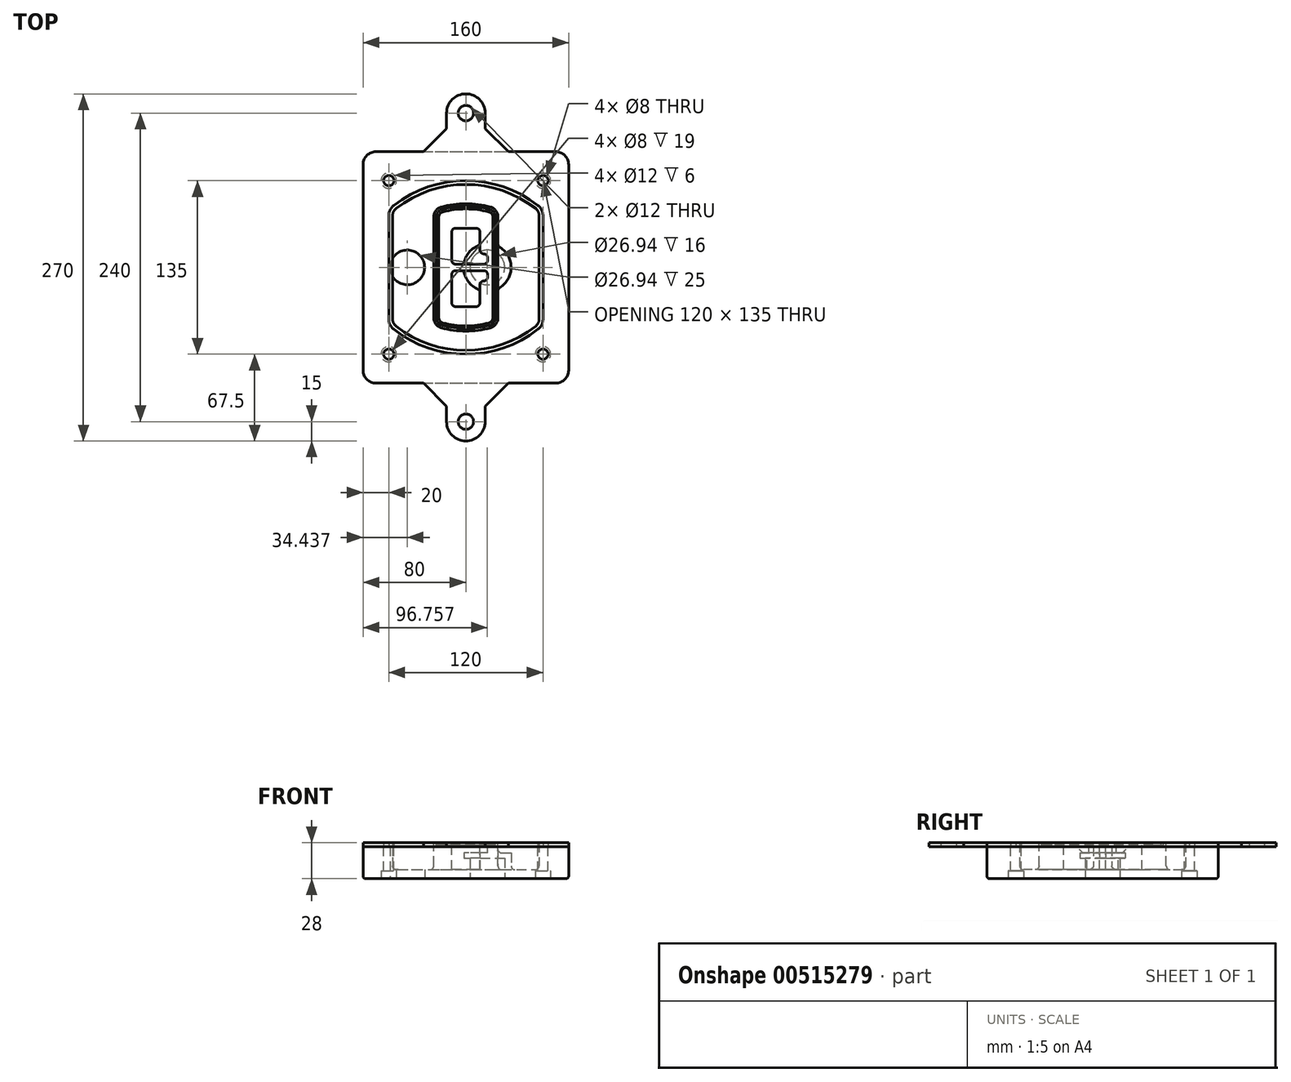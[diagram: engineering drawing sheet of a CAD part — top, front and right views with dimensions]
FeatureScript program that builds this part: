
annotation { "Feature Type Name" : "Feature", "Feature Type Description" : "" }
export const myFeature = defineFeature(function(context is Context, id is Id, definition is map)
    precondition{}
    {
        {
            var Q0;
            Q0=qCreatedBy(makeId("Top.planeOp"),FACE);
            var sketch = newSketch(context, id + "F0", { "sketchPlane" : qUnion([Q0])});
            skPoint(sketch, "E0.rect.middle", {"position": v(0, 0) * mm});
            skLineSegment(sketch, "E1.bottom", {"start": v(-70, -90) * mm, "end": v(70, -90) * mm});
            skLineSegment(sketch, "E1.top", {"start": v(-70, 90) * mm, "end": v(70, 90) * mm});
            skLineSegment(sketch, "E1.left", {"start": v(-80, -80) * mm, "end": v(-80, 80) * mm});
            skLineSegment(sketch, "E1.right", {"start": v(80, -80) * mm, "end": v(80, 80) * mm});
            skLineSegment(sketch, "E2", {"start": v(-80, 90) * mm, "end": v(80, -90) * mm, "construction": true});
            skLineSegment(sketch, "E3", {"start": v(80, 90) * mm, "end": v(-80, -90) * mm, "construction": true});
            skCircle(sketch, "E4", {"center": v(-60, 67.5) * mm, "radius": 4 * mm});
            skCircle(sketch, "E5", {"center": v(60, 67.5) * mm, "radius": 4 * mm});
            skCircle(sketch, "E6", {"center": v(60, -67.5) * mm, "radius": 4 * mm});
            skCircle(sketch, "E7", {"center": v(-60, -67.5) * mm, "radius": 4 * mm});
            skLineSegment(sketch, "E8", {"start": v(-60, 67.5) * mm, "end": v(60, 67.5) * mm, "construction": true});
            skLineSegment(sketch, "E9", {"start": v(60, 67.5) * mm, "end": v(60, -67.5) * mm, "construction": true});
            skLineSegment(sketch, "E10", {"start": v(60, -67.5) * mm, "end": v(-60, -67.5) * mm, "construction": true});
            skLineSegment(sketch, "E11", {"start": v(-60, -67.5) * mm, "end": v(-60, 67.5) * mm, "construction": true});
            skLineSegment(sketch, "E12", {"start": v(-60, 40.3) * mm, "end": v(-60, -40.3) * mm});
            skLineSegment(sketch, "E13", {"start": v(60, 40.3) * mm, "end": v(60, -40.3) * mm});
            skArc(sketch, "E14", {"start": v(56.15, 48.18) * mm, "mid": v(0, 67.5) * mm, "end": v(-56.15, 48.18) * mm});
            skArc(sketch, "E15", {"start": v(-56.15, -48.18) * mm, "mid": v(0, -67.5) * mm, "end": v(56.15, -48.18) * mm});
            skLineSegment(sketch, "E16", {"start": v(-60, 0) * mm, "end": v(60, 0) * mm, "construction": true});
            skPoint(sketch, "E17.visualSharp", {"position": v(-60, -45) * mm});
            skArc(sketch, "E17.filletArc", {"start": v(-60, -40.3) * mm, "mid": v(-58.99, -44.68) * mm, "end": v(-56.15, -48.18) * mm});
            skPoint(sketch, "E18.visualSharp", {"position": v(-60, 45) * mm});
            skArc(sketch, "E18.filletArc", {"start": v(-56.15, 48.18) * mm, "mid": v(-58.99, 44.68) * mm, "end": v(-60, 40.3) * mm});
            skPoint(sketch, "E19.visualSharp", {"position": v(60, 45) * mm});
            skArc(sketch, "E19.filletArc", {"start": v(60, 40.3) * mm, "mid": v(58.99, 44.68) * mm, "end": v(56.15, 48.18) * mm});
            skPoint(sketch, "E20.visualSharp", {"position": v(60, -45) * mm});
            skArc(sketch, "E20.filletArc", {"start": v(56.15, -48.18) * mm, "mid": v(58.99, -44.68) * mm, "end": v(60, -40.3) * mm});
            skPoint(sketch, "E21.visualSharp", {"position": v(-80, 90) * mm});
            skArc(sketch, "E21.filletArc", {"start": v(-70, 90) * mm, "mid": v(-77.07, 87.07) * mm, "end": v(-80, 80) * mm});
            skPoint(sketch, "E22.visualSharp", {"position": v(80, 90) * mm});
            skArc(sketch, "E22.filletArc", {"start": v(80, 80) * mm, "mid": v(77.07, 87.07) * mm, "end": v(70, 90) * mm});
            skPoint(sketch, "E23.visualSharp", {"position": v(80, -90) * mm});
            skArc(sketch, "E23.filletArc", {"start": v(70, -90) * mm, "mid": v(77.07, -87.07) * mm, "end": v(80, -80) * mm});
            skPoint(sketch, "E24.visualSharp", {"position": v(-80, -90) * mm});
            skArc(sketch, "E24.filletArc", {"start": v(-80, -80) * mm, "mid": v(-77.07, -87.07) * mm, "end": v(-70, -90) * mm});
            skArc(sketch, "E25.0", {"start": v(57, 40.3) * mm, "mid": v(56.3, 43.36) * mm, "end": v(54.3, 45.81) * mm});
            skLineSegment(sketch, "E25.1", {"start": v(57, 40.3) * mm, "end": v(57, -40.3) * mm});
            skArc(sketch, "E25.2", {"start": v(54.3, -45.81) * mm, "mid": v(56.3, -43.36) * mm, "end": v(57, -40.3) * mm});
            skArc(sketch, "E25.3", {"start": v(-54.3, -45.81) * mm, "mid": v(0, -64.5) * mm, "end": v(54.3, -45.81) * mm});
            skArc(sketch, "E25.4", {"start": v(-57, -40.3) * mm, "mid": v(-56.3, -43.36) * mm, "end": v(-54.3, -45.81) * mm});
            skArc(sketch, "E25.5", {"start": v(54.3, 45.81) * mm, "mid": v(0, 64.5) * mm, "end": v(-54.3, 45.81) * mm});
            skLineSegment(sketch, "E25.6", {"start": v(-57, 40.3) * mm, "end": v(-57, -40.3) * mm});
            skArc(sketch, "E25.7", {"start": v(-54.3, 45.81) * mm, "mid": v(-56.3, 43.36) * mm, "end": v(-57, 40.3) * mm});
            skArc(sketch, "E26.0", {"start": v(-58.62, 51.33) * mm, "mid": v(-62.58, 46.43) * mm, "end": v(-64, 40.3) * mm});
            skArc(sketch, "E26.1", {"start": v(58.62, 51.33) * mm, "mid": v(0, 71.5) * mm, "end": v(-58.62, 51.33) * mm});
            skArc(sketch, "E26.2", {"start": v(64, 40.3) * mm, "mid": v(62.58, 46.43) * mm, "end": v(58.62, 51.33) * mm});
            skLineSegment(sketch, "E26.3", {"start": v(64, 40.3) * mm, "end": v(64, -40.3) * mm});
            skArc(sketch, "E26.4", {"start": v(58.62, -51.33) * mm, "mid": v(62.58, -46.43) * mm, "end": v(64, -40.3) * mm});
            skLineSegment(sketch, "E26.5", {"start": v(-64, 40.3) * mm, "end": v(-64, -40.3) * mm});
            skArc(sketch, "E26.6", {"start": v(-58.62, -51.33) * mm, "mid": v(0, -71.5) * mm, "end": v(58.62, -51.33) * mm});
            skArc(sketch, "E26.7", {"start": v(-64, -40.3) * mm, "mid": v(-62.58, -46.43) * mm, "end": v(-58.62, -51.33) * mm});
            skSolve(sketch);
        }
        {
            var Q0;
            Q0=makeQuery(id+"F0.imprint","IMPRINT",FACE,{"disambiguationData":[TD([[makeQuery(id+"F0.imprint","IMPRINT",EDGE,{"derivedFrom":sQuery(id+"F0.wireOp",EDGE,"E1.bottom")}),1.0]])]});
            var Q1;
            Q1=makeQuery(id+"F0.imprint","IMPRINT",FACE,{"disambiguationData":[TD([[makeQuery(id+"F0.imprint","IMPRINT",EDGE,{"derivedFrom":sQuery(id+"F0.wireOp",EDGE,"E12")}),1.0]])]});
            var Q2;
            Q2=makeQuery(id+"F0.imprint","IMPRINT",FACE,{"disambiguationData":[TD([[makeQuery(id+"F0.imprint","IMPRINT",EDGE,{"derivedFrom":sQuery(id+"F0.wireOp",EDGE,"E25.0")}),1.0]])]});
            var Q3;
            Q3=makeQuery(id+"F0.imprint","IMPRINT",FACE,{"disambiguationData":[TD([[makeQuery(id+"F0.imprint","IMPRINT",EDGE,{"derivedFrom":sQuery(id+"F0.wireOp",EDGE,"E12")}),-1.0]])]});
            extrude(context, id + "F1", {"entities" : qUnion([Q0, Q1, Q2, Q3]), "oppositeDirection" : true, "depth" : 25 * mm});
        }
        {
            var Q0;
            Q0=makeQuery(id+"F0.imprint","IMPRINT",FACE,{"disambiguationData":[TD([[makeQuery(id+"F0.imprint","IMPRINT",EDGE,{"derivedFrom":sQuery(id+"F0.wireOp",EDGE,"E12")}),1.0]])]});
            extrude(context, id + "F2", {"entities" : qUnion([Q0]), "operationType" : NewBodyOperationType.ADD, "depth" : 3 * mm});
        }
        {
            var Q0;
            Q0=makeQuery(id+"F0.imprint","IMPRINT",FACE,{"disambiguationData":[TD([[makeQuery(id+"F0.imprint","IMPRINT",EDGE,{"derivedFrom":sQuery(id+"F0.wireOp",EDGE,"E25.0")}),1.0]])]});
            extrude(context, id + "F3", {"entities" : qUnion([Q0]), "operationType" : NewBodyOperationType.REMOVE, "oppositeDirection" : true, "depth" : 18 * mm});
        }
        {
            var Q0;
            Q0=makeQuery(id+"F2.opExtrude","CAP_FACE",FACE,{"disambiguationData":[OSD([sQuery(id+"F0.wireOp",EDGE,"E12"),sQuery(id+"F0.wireOp",EDGE,"E13"),sQuery(id+"F0.wireOp",EDGE,"E14"),sQuery(id+"F0.wireOp",EDGE,"E15"),sQuery(id+"F0.wireOp",EDGE,"E17.filletArc"),sQuery(id+"F0.wireOp",EDGE,"E18.filletArc"),sQuery(id+"F0.wireOp",EDGE,"E19.filletArc"),sQuery(id+"F0.wireOp",EDGE,"E20.filletArc"),sQuery(id+"F0.wireOp",EDGE,"E25.0"),sQuery(id+"F0.wireOp",EDGE,"E25.1"),sQuery(id+"F0.wireOp",EDGE,"E25.2"),sQuery(id+"F0.wireOp",EDGE,"E25.3"),sQuery(id+"F0.wireOp",EDGE,"E25.4"),sQuery(id+"F0.wireOp",EDGE,"E25.5"),sQuery(id+"F0.wireOp",EDGE,"E25.6"),sQuery(id+"F0.wireOp",EDGE,"E25.7")])],"isStart":false});
            var sketch = newSketch(context, id + "F4", { "sketchPlane" : qUnion([Q0])});
            skArc(sketch, "E27.0", {"start": v(-19.08, -46.97) * mm, "mid": v(0, -49.5) * mm, "end": v(19.08, -46.97) * mm});
            skArc(sketch, "E28.0", {"start": v(19.08, 46.97) * mm, "mid": v(0, 49.5) * mm, "end": v(-19.08, 46.97) * mm});
            skLineSegment(sketch, "E29", {"start": v(-25, 39.25) * mm, "end": v(-25, -39.25) * mm});
            skLineSegment(sketch, "E30", {"start": v(25, 39.25) * mm, "end": v(25, -39.25) * mm});
            skLineSegment(sketch, "E31", {"start": v(-25, 45.1) * mm, "end": v(25, 45.1) * mm, "construction": true});
            skLineSegment(sketch, "E32", {"start": v(-25, -45.1) * mm, "end": v(25, -45.1) * mm, "construction": true});
            skPoint(sketch, "E33.visualSharp", {"position": v(-25, 45.1) * mm});
            skArc(sketch, "E33.filletArc", {"start": v(-19.08, 46.97) * mm, "mid": v(-23.35, 44.11) * mm, "end": v(-25, 39.25) * mm});
            skPoint(sketch, "E34.visualSharp", {"position": v(25, 45.1) * mm});
            skArc(sketch, "E34.filletArc", {"start": v(25, 39.25) * mm, "mid": v(23.35, 44.11) * mm, "end": v(19.08, 46.97) * mm});
            skPoint(sketch, "E35.visualSharp", {"position": v(25, -45.1) * mm});
            skArc(sketch, "E35.filletArc", {"start": v(19.08, -46.97) * mm, "mid": v(23.35, -44.11) * mm, "end": v(25, -39.25) * mm});
            skPoint(sketch, "E36.visualSharp", {"position": v(-25, -45.1) * mm});
            skArc(sketch, "E36.filletArc", {"start": v(-25, -39.25) * mm, "mid": v(-23.35, -44.11) * mm, "end": v(-19.08, -46.97) * mm});
            skArc(sketch, "E37.0", {"start": v(54.3, 45.81) * mm, "mid": v(0, 64.5) * mm, "end": v(-54.3, 45.81) * mm});
            skArc(sketch, "E37.1", {"start": v(-54.3, 45.81) * mm, "mid": v(-56.3, 43.36) * mm, "end": v(-57, 40.3) * mm});
            skLineSegment(sketch, "E37.2", {"start": v(-57, 40.3) * mm, "end": v(-57, -40.3) * mm});
            skArc(sketch, "E37.3", {"start": v(-57, -40.3) * mm, "mid": v(-56.3, -43.36) * mm, "end": v(-54.3, -45.81) * mm});
            skArc(sketch, "E37.4", {"start": v(-54.3, -45.81) * mm, "mid": v(0, -64.5) * mm, "end": v(54.3, -45.81) * mm});
            skArc(sketch, "E37.5", {"start": v(54.3, -45.81) * mm, "mid": v(56.3, -43.36) * mm, "end": v(57, -40.3) * mm});
            skLineSegment(sketch, "E37.6", {"start": v(57, 40.3) * mm, "end": v(57, -40.3) * mm});
            skArc(sketch, "E37.7", {"start": v(57, 40.3) * mm, "mid": v(56.3, 43.36) * mm, "end": v(54.3, 45.81) * mm});
            skLineSegment(sketch, "E38.0", {"start": v(23, 39.25) * mm, "end": v(23, -39.25) * mm});
            skArc(sketch, "E38.1", {"start": v(18.56, -45.04) * mm, "mid": v(21.76, -42.9) * mm, "end": v(23, -39.25) * mm});
            skArc(sketch, "E38.2", {"start": v(-18.56, -45.04) * mm, "mid": v(0, -47.5) * mm, "end": v(18.56, -45.04) * mm});
            skArc(sketch, "E38.3", {"start": v(-23, -39.25) * mm, "mid": v(-21.76, -42.9) * mm, "end": v(-18.56, -45.04) * mm});
            skLineSegment(sketch, "E38.4", {"start": v(-23, 39.25) * mm, "end": v(-23, -39.25) * mm});
            skArc(sketch, "E38.5", {"start": v(23, 39.25) * mm, "mid": v(21.76, 42.9) * mm, "end": v(18.56, 45.04) * mm});
            skArc(sketch, "E38.6", {"start": v(-18.56, 45.04) * mm, "mid": v(-21.76, 42.9) * mm, "end": v(-23, 39.25) * mm});
            skArc(sketch, "E38.7", {"start": v(18.56, 45.04) * mm, "mid": v(0, 47.5) * mm, "end": v(-18.56, 45.04) * mm});
            skArc(sketch, "E39.0", {"start": v(21, 39.25) * mm, "mid": v(20.18, 41.68) * mm, "end": v(18.04, 43.1) * mm});
            skLineSegment(sketch, "E39.1", {"start": v(21, 39.25) * mm, "end": v(21, -39.25) * mm});
            skArc(sketch, "E39.2", {"start": v(18.04, -43.1) * mm, "mid": v(20.18, -41.68) * mm, "end": v(21, -39.25) * mm});
            skArc(sketch, "E39.3", {"start": v(-18.04, -43.1) * mm, "mid": v(0, -45.5) * mm, "end": v(18.04, -43.1) * mm});
            skArc(sketch, "E39.4", {"start": v(-21, -39.25) * mm, "mid": v(-20.18, -41.68) * mm, "end": v(-18.04, -43.1) * mm});
            skArc(sketch, "E39.5", {"start": v(18.04, 43.1) * mm, "mid": v(0, 45.5) * mm, "end": v(-18.04, 43.1) * mm});
            skLineSegment(sketch, "E39.6", {"start": v(-21, 39.25) * mm, "end": v(-21, -39.25) * mm});
            skArc(sketch, "E39.7", {"start": v(-18.04, 43.1) * mm, "mid": v(-20.18, 41.68) * mm, "end": v(-21, 39.25) * mm});
            skLineSegment(sketch, "E40", {"start": v(-25, 0) * mm, "end": v(25, 0) * mm, "construction": true});
            skLineSegment(sketch, "E41", {"start": v(-11, 5.5) * mm, "end": v(-11, 27.5) * mm});
            skLineSegment(sketch, "E42", {"start": v(-8, 30.5) * mm, "end": v(8, 30.5) * mm});
            skLineSegment(sketch, "E43", {"start": v(11, 27.5) * mm, "end": v(11, 13.5) * mm});
            skLineSegment(sketch, "E44", {"start": v(14, 10.5) * mm, "end": v(14, 10.5) * mm});
            skLineSegment(sketch, "E45", {"start": v(17, 7.5) * mm, "end": v(17, 5.5) * mm});
            skLineSegment(sketch, "E46", {"start": v(14, 2.5) * mm, "end": v(-8, 2.5) * mm});
            skPoint(sketch, "E47.visualSharp", {"position": v(-11, 30.5) * mm});
            skArc(sketch, "E47.filletArc", {"start": v(-8, 30.5) * mm, "mid": v(-10.12, 29.62) * mm, "end": v(-11, 27.5) * mm});
            skPoint(sketch, "E48.visualSharp", {"position": v(11, 30.5) * mm});
            skArc(sketch, "E48.filletArc", {"start": v(11, 27.5) * mm, "mid": v(10.12, 29.62) * mm, "end": v(8, 30.5) * mm});
            skPoint(sketch, "E49.visualSharp", {"position": v(11, 10.5) * mm});
            skArc(sketch, "E49.filletArc", {"start": v(11, 13.5) * mm, "mid": v(11.88, 11.38) * mm, "end": v(14, 10.5) * mm});
            skPoint(sketch, "E50.visualSharp", {"position": v(17, 10.5) * mm});
            skArc(sketch, "E50.filletArc", {"start": v(17, 7.5) * mm, "mid": v(16.12, 9.62) * mm, "end": v(14, 10.5) * mm});
            skPoint(sketch, "E51.visualSharp", {"position": v(17, 2.5) * mm});
            skArc(sketch, "E51.filletArc", {"start": v(14, 2.5) * mm, "mid": v(16.12, 3.38) * mm, "end": v(17, 5.5) * mm});
            skPoint(sketch, "E52.visualSharp", {"position": v(-11, 2.5) * mm});
            skArc(sketch, "E52.filletArc", {"start": v(-11, 5.5) * mm, "mid": v(-10.12, 3.38) * mm, "end": v(-8, 2.5) * mm});
            skLineSegment(sketch, "E53.0.MirrorCS", {"start": v(14, -2.5) * mm, "end": v(-8, -2.5) * mm});
            skArc(sketch, "E54.0.MirrorCS", {"start": v(-11, -5.5) * mm, "mid": v(-10.12, -3.38) * mm, "end": v(-8, -2.5) * mm});
            skLineSegment(sketch, "E55.0.MirrorCS", {"start": v(-11, -5.5) * mm, "end": v(-11, -27.5) * mm});
            skArc(sketch, "E56.0.MirrorCS", {"start": v(-8, -30.5) * mm, "mid": v(-10.12, -29.62) * mm, "end": v(-11, -27.5) * mm});
            skLineSegment(sketch, "E57.0.MirrorCS", {"start": v(-8, -30.5) * mm, "end": v(8, -30.5) * mm});
            skArc(sketch, "E58.0.MirrorCS", {"start": v(11, -27.5) * mm, "mid": v(10.12, -29.62) * mm, "end": v(8, -30.5) * mm});
            skLineSegment(sketch, "E59.0.MirrorCS", {"start": v(11, -27.5) * mm, "end": v(11, -13.5) * mm});
            skArc(sketch, "E60.0.MirrorCS", {"start": v(11, -13.5) * mm, "mid": v(11.88, -11.38) * mm, "end": v(14, -10.5) * mm});
            skArc(sketch, "E61.0.MirrorCS", {"start": v(17, -7.5) * mm, "mid": v(16.12, -9.62) * mm, "end": v(14, -10.5) * mm});
            skLineSegment(sketch, "E62.0.MirrorCS", {"start": v(17, -7.5) * mm, "end": v(17, -5.5) * mm});
            skArc(sketch, "E63.0.MirrorCS", {"start": v(14, -2.5) * mm, "mid": v(16.12, -3.38) * mm, "end": v(17, -5.5) * mm});
            skSolve(sketch);
        }
        {
            var Q0;
            Q0=makeQuery(id+"F4.imprint","IMPRINT",FACE,{"disambiguationData":[TD([[makeQuery(id+"F4.imprint","IMPRINT",EDGE,{"derivedFrom":sQuery(id+"F4.wireOp",EDGE,"E27.0")}),1.0]])]});
            var Q1;
            Q1=makeQuery(id+"F4.imprint","IMPRINT",FACE,{"disambiguationData":[TD([[makeQuery(id+"F4.imprint","IMPRINT",EDGE,{"derivedFrom":sQuery(id+"F4.wireOp",EDGE,"E38.0")}),-1.0]])]});
            var Q2;
            Q2=makeQuery(id+"F4.imprint","IMPRINT",FACE,{"disambiguationData":[TD([[makeQuery(id+"F4.imprint","IMPRINT",EDGE,{"derivedFrom":sQuery(id+"F4.wireOp",EDGE,"E39.0")}),1.0]])]});
            extrude(context, id + "F5", {"entities" : qUnion([Q0, Q1, Q2]), "operationType" : NewBodyOperationType.ADD, "endBound" : BoundingType.UP_TO_NEXT, "oppositeDirection" : true, "depth" : 25 * mm});
        }
        {
            var Q0;
            Q0=makeQuery(id+"F4.imprint","IMPRINT",FACE,{"disambiguationData":[TD([[makeQuery(id+"F4.imprint","IMPRINT",EDGE,{"derivedFrom":sQuery(id+"F4.wireOp",EDGE,"E38.0")}),-1.0]])]});
            extrude(context, id + "F6", {"entities" : qUnion([Q0]), "operationType" : NewBodyOperationType.REMOVE, "oppositeDirection" : true, "depth" : 2 * mm});
        }
        {
            var Q0;
            Q0=makeQuery(id+"F1.opExtrude","CAP_FACE",FACE,{"disambiguationData":[OSD([sQuery(id+"F0.wireOp",EDGE,"E1.bottom"),sQuery(id+"F0.wireOp",EDGE,"E1.top"),sQuery(id+"F0.wireOp",EDGE,"E1.left"),sQuery(id+"F0.wireOp",EDGE,"E1.right"),sQuery(id+"F0.wireOp",EDGE,"E4"),sQuery(id+"F0.wireOp",EDGE,"E5"),sQuery(id+"F0.wireOp",EDGE,"E6"),sQuery(id+"F0.wireOp",EDGE,"E7"),sQuery(id+"F0.wireOp",EDGE,"E21.filletArc"),sQuery(id+"F0.wireOp",EDGE,"E22.filletArc"),sQuery(id+"F0.wireOp",EDGE,"E23.filletArc"),sQuery(id+"F0.wireOp",EDGE,"E24.filletArc")])],"isStart":false});
            var sketch = newSketch(context, id + "F7", { "sketchPlane" : qUnion([Q0])});
            skCircle(sketch, "E64", {"center": v(16.76, 0) * mm, "radius": 13.47 * mm});
            skCircle(sketch, "E65", {"center": v(-45.56, 0) * mm, "radius": 13.47 * mm});
            skLineSegment(sketch, "E66", {"start": v(80, 0) * mm, "end": v(-80, 0) * mm});
            skCircle(sketch, "E67", {"center": v(16.76, 0) * mm, "radius": 18.47 * mm});
            skCircle(sketch, "E68", {"center": v(60, -67.5) * mm, "radius": 6 * mm});
            skCircle(sketch, "E69", {"center": v(-60, -67.5) * mm, "radius": 6 * mm});
            skCircle(sketch, "E70", {"center": v(-60, 67.5) * mm, "radius": 6 * mm});
            skCircle(sketch, "E71", {"center": v(60, 67.5) * mm, "radius": 6 * mm});
            skSolve(sketch);
        }
        {
            var Q0;
            {var subQ1=sQuery(id+"F7.wireOp",EDGE,"E66");var subQ4=sQuery(id+"F7.wireOp",EDGE,"E64");var subQ6=makeQuery(id+"F7.imprint","INTERSECT",VERTEX,{"disambiguationData":[OD(0.0)],"derivedFrom":[subQ4,subQ1]});Q0=makeQuery(id+"F7.imprint","IMPRINT",FACE,{"disambiguationData":[TD([[makeQuery(id+"F7.imprint","IMPRINT",EDGE,{"disambiguationData":[TD([[subQ6,-1.0]])],"derivedFrom":subQ4}),-1.0]])]});}
            var Q1;
            {var subQ0=sQuery(id+"F7.wireOp",EDGE,"E66");var subQ1=sQuery(id+"F7.wireOp",EDGE,"E64");var subQ3=makeQuery(id+"F7.imprint","INTERSECT",VERTEX,{"disambiguationData":[OD(0.0)],"derivedFrom":[subQ1,subQ0]});Q1=makeQuery(id+"F7.imprint","IMPRINT",FACE,{"disambiguationData":[TD([[makeQuery(id+"F7.imprint","IMPRINT",EDGE,{"disambiguationData":[TD([[subQ3,-1.0]])],"derivedFrom":subQ1}),1.0]])]});}
            var Q2;
            {var subQ0=sQuery(id+"F7.wireOp",EDGE,"E66");var subQ1=sQuery(id+"F7.wireOp",EDGE,"E64");var subQ3=makeQuery(id+"F7.imprint","INTERSECT",VERTEX,{"disambiguationData":[OD(0.0)],"derivedFrom":[subQ1,subQ0]});Q2=makeQuery(id+"F7.imprint","IMPRINT",FACE,{"disambiguationData":[TD([[makeQuery(id+"F7.imprint","IMPRINT",EDGE,{"disambiguationData":[TD([[subQ3,1.0]])],"derivedFrom":subQ1}),1.0]])]});}
            var Q3;
            {var subQ1=sQuery(id+"F7.wireOp",EDGE,"E66");var subQ4=sQuery(id+"F7.wireOp",EDGE,"E64");var subQ6=makeQuery(id+"F7.imprint","INTERSECT",VERTEX,{"disambiguationData":[OD(0.0)],"derivedFrom":[subQ4,subQ1]});Q3=makeQuery(id+"F7.imprint","IMPRINT",FACE,{"disambiguationData":[TD([[makeQuery(id+"F7.imprint","IMPRINT",EDGE,{"disambiguationData":[TD([[subQ6,1.0]])],"derivedFrom":subQ4}),-1.0]])]});}
            extrude(context, id + "F8", {"entities" : qUnion([Q0, Q1, Q2, Q3]), "operationType" : NewBodyOperationType.ADD, "oppositeDirection" : true, "depth" : 20 * mm});
        }
        {
            var Q0;
            {var subQ0=sQuery(id+"F7.wireOp",EDGE,"E66");var subQ1=sQuery(id+"F7.wireOp",EDGE,"E64");var subQ3=makeQuery(id+"F7.imprint","INTERSECT",VERTEX,{"disambiguationData":[OD(0.0)],"derivedFrom":[subQ1,subQ0]});Q0=makeQuery(id+"F7.imprint","IMPRINT",FACE,{"disambiguationData":[TD([[makeQuery(id+"F7.imprint","IMPRINT",EDGE,{"disambiguationData":[TD([[subQ3,-1.0]])],"derivedFrom":subQ1}),1.0]])]});}
            var Q1;
            {var subQ0=sQuery(id+"F7.wireOp",EDGE,"E66");var subQ1=sQuery(id+"F7.wireOp",EDGE,"E64");var subQ3=makeQuery(id+"F7.imprint","INTERSECT",VERTEX,{"disambiguationData":[OD(0.0)],"derivedFrom":[subQ1,subQ0]});Q1=makeQuery(id+"F7.imprint","IMPRINT",FACE,{"disambiguationData":[TD([[makeQuery(id+"F7.imprint","IMPRINT",EDGE,{"disambiguationData":[TD([[subQ3,1.0]])],"derivedFrom":subQ1}),1.0]])]});}
            extrude(context, id + "F9", {"entities" : qUnion([Q0, Q1]), "operationType" : NewBodyOperationType.REMOVE, "oppositeDirection" : true, "depth" : 16 * mm});
        }
        {
            var Q0;
            {var subQ0=sQuery(id+"F7.wireOp",EDGE,"E66");var subQ1=sQuery(id+"F7.wireOp",EDGE,"E65");var subQ3=makeQuery(id+"F7.imprint","INTERSECT",VERTEX,{"disambiguationData":[OD(0.0)],"derivedFrom":[subQ1,subQ0]});Q0=makeQuery(id+"F7.imprint","IMPRINT",FACE,{"disambiguationData":[TD([[makeQuery(id+"F7.imprint","IMPRINT",EDGE,{"disambiguationData":[TD([[subQ3,-1.0]])],"derivedFrom":subQ1}),1.0]])]});}
            var Q1;
            {var subQ0=sQuery(id+"F7.wireOp",EDGE,"E66");var subQ1=sQuery(id+"F7.wireOp",EDGE,"E65");var subQ3=makeQuery(id+"F7.imprint","INTERSECT",VERTEX,{"disambiguationData":[OD(0.0)],"derivedFrom":[subQ1,subQ0]});Q1=makeQuery(id+"F7.imprint","IMPRINT",FACE,{"disambiguationData":[TD([[makeQuery(id+"F7.imprint","IMPRINT",EDGE,{"disambiguationData":[TD([[subQ3,1.0]])],"derivedFrom":subQ1}),1.0]])]});}
            extrude(context, id + "F10", {"entities" : qUnion([Q0, Q1]), "operationType" : NewBodyOperationType.REMOVE, "oppositeDirection" : true, "depth" : 25 * mm});
        }
        {
            var Q0;
            Q0=makeQuery(id+"F7.imprint","IMPRINT",FACE,{"disambiguationData":[TD([[makeQuery(id+"F7.imprint","IMPRINT",EDGE,{"derivedFrom":sQuery(id+"F7.wireOp",EDGE,"E68")}),1.0]])]});
            var Q1;
            Q1=makeQuery(id+"F7.imprint","IMPRINT",FACE,{"disambiguationData":[TD([[makeQuery(id+"F7.imprint","IMPRINT",EDGE,{"derivedFrom":makeQuery(id+"F1.opExtrude","CAP_EDGE",EDGE,{"disambiguationData":[OSD([sQuery(id+"F0.wireOp",EDGE,"E5")])],"isStart":false})}),-1.0]])]});
            var Q2;
            Q2=makeQuery(id+"F7.imprint","IMPRINT",FACE,{"disambiguationData":[TD([[makeQuery(id+"F7.imprint","IMPRINT",EDGE,{"derivedFrom":sQuery(id+"F7.wireOp",EDGE,"E69")}),1.0]])]});
            var Q3;
            Q3=makeQuery(id+"F7.imprint","IMPRINT",FACE,{"disambiguationData":[TD([[makeQuery(id+"F7.imprint","IMPRINT",EDGE,{"derivedFrom":makeQuery(id+"F1.opExtrude","CAP_EDGE",EDGE,{"disambiguationData":[OSD([sQuery(id+"F0.wireOp",EDGE,"E4")])],"isStart":false})}),-1.0]])]});
            var Q4;
            Q4=makeQuery(id+"F7.imprint","IMPRINT",FACE,{"disambiguationData":[TD([[makeQuery(id+"F7.imprint","IMPRINT",EDGE,{"derivedFrom":sQuery(id+"F7.wireOp",EDGE,"E70")}),1.0]])]});
            var Q5;
            Q5=makeQuery(id+"F7.imprint","IMPRINT",FACE,{"disambiguationData":[TD([[makeQuery(id+"F7.imprint","IMPRINT",EDGE,{"derivedFrom":makeQuery(id+"F1.opExtrude","CAP_EDGE",EDGE,{"disambiguationData":[OSD([sQuery(id+"F0.wireOp",EDGE,"E7")])],"isStart":false})}),-1.0]])]});
            var Q6;
            Q6=makeQuery(id+"F7.imprint","IMPRINT",FACE,{"disambiguationData":[TD([[makeQuery(id+"F7.imprint","IMPRINT",EDGE,{"derivedFrom":sQuery(id+"F7.wireOp",EDGE,"E71")}),1.0]])]});
            var Q7;
            Q7=makeQuery(id+"F7.imprint","IMPRINT",FACE,{"disambiguationData":[TD([[makeQuery(id+"F7.imprint","IMPRINT",EDGE,{"derivedFrom":makeQuery(id+"F1.opExtrude","CAP_EDGE",EDGE,{"disambiguationData":[OSD([sQuery(id+"F0.wireOp",EDGE,"E6")])],"isStart":false})}),-1.0]])]});
            extrude(context, id + "F11", {"entities" : qUnion([Q0, Q1, Q2, Q3, Q4, Q5, Q6, Q7]), "operationType" : NewBodyOperationType.REMOVE, "oppositeDirection" : true, "depth" : 6 * mm});
        }
        {
            var Q0;
            Q0=makeQuery(id+"F9.boolean.opBoolean","COPY",FACE,{"derivedFrom":makeQuery(id+"F9.opExtrude","CAP_FACE",FACE,{"disambiguationData":[OSD([sQuery(id+"F7.wireOp",EDGE,"E64")])],"isStart":false})});
            var sketch = newSketch(context, id + "F12", { "sketchPlane" : qUnion([Q0])});
            skArc(sketch, "E72.0", {"start": v(11, 17.55) * mm, "mid": v(2.57, 11.82) * mm, "end": v(-1.54, 2.5) * mm});
            skArc(sketch, "E72.1", {"start": v(-1.54, -2.5) * mm, "mid": v(2.57, -11.82) * mm, "end": v(11, -17.55) * mm});
            skLineSegment(sketch, "E73", {"start": v(-1.54, -2.5) * mm, "end": v(14, -2.5) * mm});
            skLineSegment(sketch, "E74.0", {"start": v(14, 2.5) * mm, "end": v(-1.54, 2.5) * mm});
            skArc(sketch, "E74.1", {"start": v(14, 2.5) * mm, "mid": v(16.12, 3.38) * mm, "end": v(17, 5.5) * mm});
            skLineSegment(sketch, "E74.2", {"start": v(17, 7.5) * mm, "end": v(17, 5.5) * mm});
            skArc(sketch, "E74.3", {"start": v(17, 7.5) * mm, "mid": v(16.12, 9.62) * mm, "end": v(14, 10.5) * mm});
            skArc(sketch, "E74.4", {"start": v(11, 13.5) * mm, "mid": v(11.88, 11.38) * mm, "end": v(14, 10.5) * mm});
            skLineSegment(sketch, "E74.5", {"start": v(11, 17.55) * mm, "end": v(11, 13.5) * mm});
            skLineSegment(sketch, "E74.7", {"start": v(14, -2.5) * mm, "end": v(-1.54, -2.5) * mm});
            skArc(sketch, "E74.8", {"start": v(14, -2.5) * mm, "mid": v(16.12, -3.38) * mm, "end": v(17, -5.5) * mm});
            skLineSegment(sketch, "E74.9", {"start": v(17, -7.5) * mm, "end": v(17, -5.5) * mm});
            skArc(sketch, "E74.10", {"start": v(17, -7.5) * mm, "mid": v(16.12, -9.62) * mm, "end": v(14, -10.5) * mm});
            skArc(sketch, "E74.11", {"start": v(11, -13.5) * mm, "mid": v(11.88, -11.38) * mm, "end": v(14, -10.5) * mm});
            skLineSegment(sketch, "E74.12", {"start": v(11, -17.55) * mm, "end": v(11, -13.5) * mm});
            skPoint(sketch, "E75.orphan", {"position": v(11, -27.5) * mm});
            skPoint(sketch, "E76.orphan", {"position": v(-8, -2.5) * mm});
            skPoint(sketch, "E77.orphan", {"position": v(-8, 2.5) * mm});
            skPoint(sketch, "E78.orphan", {"position": v(11, 27.5) * mm});
            skSolve(sketch);
        }
        {
            var Q0;
            {var subQ7=sQuery(id+"F12.wireOp",EDGE,"E72.0");var subQ14=sQuery(id+"F12.wireOp",EDGE,"E72.1");var subQ16=sQuery(id+"F12.wireOp",EDGE,"E74.1");var subQ18=sQuery(id+"F12.wireOp",EDGE,"E74.8");Q0=qUnion([makeQuery(id+"F12.imprint","IMPRINT",FACE,{"disambiguationData":[TD([[makeQuery(id+"F12.imprint","IMPRINT",EDGE,{"derivedFrom":subQ7}),1.0]])]}),makeQuery(id+"F12.imprint","IMPRINT",FACE,{"disambiguationData":[TD([[makeQuery(id+"F12.imprint","IMPRINT",EDGE,{"derivedFrom":subQ14}),1.0]])]}),makeQuery(id+"F12.imprint","IMPRINT",FACE,{"disambiguationData":[TD([[makeQuery(id+"F12.imprint","IMPRINT",EDGE,{"derivedFrom":subQ16}),1.0]])]}),makeQuery(id+"F12.imprint","IMPRINT",FACE,{"disambiguationData":[TD([[makeQuery(id+"F12.imprint","IMPRINT",EDGE,{"derivedFrom":subQ18}),-1.0]])]})]);}
            var Q1;
            Q1=makeQuery(id+"F5.boolean.opBoolean","SPLIT",FACE,{"disambiguationData":[TD([makeQuery(id+"F5.opExtrude","SWEPT_FACE",FACE,{"disambiguationData":[OSD([sQuery(id+"F4.wireOp",EDGE,"E41")])]})])],"derivedFrom":makeQuery(id+"F3.boolean.opBoolean","COPY",FACE,{"derivedFrom":makeQuery(id+"F3.opExtrude","CAP_FACE",FACE,{"disambiguationData":[OSD([sQuery(id+"F0.wireOp",EDGE,"E25.0"),sQuery(id+"F0.wireOp",EDGE,"E25.1"),sQuery(id+"F0.wireOp",EDGE,"E25.2"),sQuery(id+"F0.wireOp",EDGE,"E25.3"),sQuery(id+"F0.wireOp",EDGE,"E25.4"),sQuery(id+"F0.wireOp",EDGE,"E25.5"),sQuery(id+"F0.wireOp",EDGE,"E25.6"),sQuery(id+"F0.wireOp",EDGE,"E25.7")])],"isStart":false})})});
            extrude(context, id + "F13", {"entities" : qUnion([Q0]), "operationType" : NewBodyOperationType.REMOVE, "endBound" : BoundingType.UP_TO_SURFACE, "endBoundEntityFace" : qUnion([Q1]), "depth" : 25 * mm});
        }
        {
            var Q0;
            Q0=makeQuery(id+"F3.boolean.opBoolean","COPY",EDGE,{"derivedFrom":makeQuery(id+"F3.opExtrude","CAP_EDGE",EDGE,{"disambiguationData":[OSD([sQuery(id+"F0.wireOp",EDGE,"E25.6")])],"isStart":false})});
            var Q1;
            Q1=makeQuery(id+"F8.boolean.opBoolean","INTERSECT",EDGE,{"derivedFrom":[makeQuery(id+"F5.opExtrude","SWEPT_FACE",FACE,{"disambiguationData":[OSD([sQuery(id+"F4.wireOp",EDGE,"E30")])]}),makeQuery(id+"F8.opExtrude","CAP_FACE",FACE,{"disambiguationData":[OSD([sQuery(id+"F7.wireOp",EDGE,"E67")])],"isStart":false})]});
            var Q2;
            Q2=makeQuery(id+"F8.boolean.opBoolean","INTERSECT",EDGE,{"disambiguationData":[OD(1.0)],"derivedFrom":[makeQuery(id+"F5.opExtrude","SWEPT_FACE",FACE,{"disambiguationData":[OSD([sQuery(id+"F4.wireOp",EDGE,"E30")])]}),makeQuery(id+"F8.opExtrude","SWEPT_FACE",FACE,{"disambiguationData":[OSD([sQuery(id+"F7.wireOp",EDGE,"E67")])]})]});
            var Q3;
            {var subQ0=sQuery(id+"F4.wireOp",EDGE,"E30");Q3=makeQuery(id+"F8.boolean.opBoolean","SPLIT",EDGE,{"disambiguationData":[TD([makeQuery(id+"F5.opExtrude","SWEPT_FACE",FACE,{"disambiguationData":[OSD([sQuery(id+"F4.wireOp",EDGE,"E35.filletArc")])]})])],"derivedFrom":makeQuery(id+"F5.opExtrude","CAP_EDGE",EDGE,{"disambiguationData":[OSD([subQ0])],"isStart":false})});}
            var Q4;
            {var subQ0=sQuery(id+"F0.wireOp",EDGE,"E25.7");var subQ1=sQuery(id+"F0.wireOp",EDGE,"E25.1");var subQ2=sQuery(id+"F0.wireOp",EDGE,"E25.6");var subQ3=sQuery(id+"F0.wireOp",EDGE,"E25.5");var subQ4=sQuery(id+"F0.wireOp",EDGE,"E25.4");var subQ5=sQuery(id+"F0.wireOp",EDGE,"E25.0");var subQ6=sQuery(id+"F0.wireOp",EDGE,"E25.2");var subQ7=sQuery(id+"F0.wireOp",EDGE,"E25.3");Q4=makeQuery(id+"F8.boolean.opBoolean","INTERSECT",EDGE,{"derivedFrom":[makeQuery(id+"F5.boolean.opBoolean","SPLIT",FACE,{"disambiguationData":[TD([makeQuery(id+"F2.opExtrude","SWEPT_FACE",FACE,{"disambiguationData":[OSD([subQ5])]})])],"derivedFrom":makeQuery(id+"F3.boolean.opBoolean","COPY",FACE,{"derivedFrom":makeQuery(id+"F3.opExtrude","CAP_FACE",FACE,{"disambiguationData":[OSD([subQ5,subQ1,subQ6,subQ7,subQ4,subQ3,subQ2,subQ0])],"isStart":false})})}),makeQuery(id+"F8.opExtrude","SWEPT_FACE",FACE,{"disambiguationData":[OSD([sQuery(id+"F7.wireOp",EDGE,"E67")])]})]});}
            var Q5;
            Q5=makeQuery(id+"F8.boolean.opBoolean","INTERSECT",EDGE,{"disambiguationData":[OD(0.0)],"derivedFrom":[makeQuery(id+"F5.opExtrude","SWEPT_FACE",FACE,{"disambiguationData":[OSD([sQuery(id+"F4.wireOp",EDGE,"E30")])]}),makeQuery(id+"F8.opExtrude","SWEPT_FACE",FACE,{"disambiguationData":[OSD([sQuery(id+"F7.wireOp",EDGE,"E67")])]})]});
            fillet(context, id + "F14", {"entities" : qUnion([Q0, Q1, Q2, Q3, Q4, Q5]), "radius" : 3 * mm, "tangentPropagation" : true, "allowEdgeOverflow" : false});
        }
        {
            var Q0;
            Q0=makeQuery(id+"F1.opExtrude","CAP_EDGE",EDGE,{"disambiguationData":[OSD([sQuery(id+"F0.wireOp",EDGE,"E1.bottom")])],"isStart":false});
            fillet(context, id + "F15", {"entities" : qUnion([Q0]), "radius" : 2 * mm, "tangentPropagation" : true, "allowEdgeOverflow" : false});
        }
        {
            var Q0;
            {var subQ0=sQuery(id+"F0.wireOp",EDGE,"E21.filletArc");var subQ1=sQuery(id+"F0.wireOp",EDGE,"E7");var subQ2=sQuery(id+"F0.wireOp",EDGE,"E6");var subQ3=sQuery(id+"F0.wireOp",EDGE,"E5");var subQ4=sQuery(id+"F0.wireOp",EDGE,"E4");var subQ5=sQuery(id+"F0.wireOp",EDGE,"E22.filletArc");var subQ6=sQuery(id+"F0.wireOp",EDGE,"E1.bottom");var subQ7=sQuery(id+"F0.wireOp",EDGE,"E1.right");var subQ8=sQuery(id+"F0.wireOp",EDGE,"E1.top");var subQ9=sQuery(id+"F0.wireOp",EDGE,"E1.left");var subQ10=sQuery(id+"F0.wireOp",EDGE,"E23.filletArc");var subQ11=sQuery(id+"F0.wireOp",EDGE,"E24.filletArc");Q0=makeQuery(id+"F2.boolean.opBoolean","SPLIT",FACE,{"disambiguationData":[TD([makeQuery(id+"F1.opExtrude","SWEPT_FACE",FACE,{"disambiguationData":[OSD([subQ6])]})])],"derivedFrom":makeQuery(id+"F1.opExtrude","CAP_FACE",FACE,{"disambiguationData":[OSD([subQ6,subQ8,subQ9,subQ7,subQ4,subQ3,subQ2,subQ1,subQ0,subQ5,subQ10,subQ11])],"isStart":true})});}
            var sketch = newSketch(context, id + "F16", { "sketchPlane" : qUnion([Q0])});
            skLineSegment(sketch, "E79", {"start": v(0, 90) * mm, "end": v(0, 120) * mm});
            skCircle(sketch, "E80", {"center": v(0, 120) * mm, "radius": 6 * mm});
            skLineSegment(sketch, "E81", {"start": v(0, 90) * mm, "end": v(-33, 90) * mm});
            skLineSegment(sketch, "E82", {"start": v(0, 90) * mm, "end": v(33, 90) * mm});
            skArc(sketch, "E83", {"start": v(-15, 120) * mm, "mid": v(0, 135) * mm, "end": v(15, 120) * mm});
            skLineSegment(sketch, "E84", {"start": v(-15, 120) * mm, "end": v(-15, 108) * mm});
            skLineSegment(sketch, "E85", {"start": v(15, 120) * mm, "end": v(15, 108) * mm});
            skLineSegment(sketch, "E86", {"start": v(-15, 108) * mm, "end": v(-33, 90) * mm});
            skLineSegment(sketch, "E87", {"start": v(15, 108) * mm, "end": v(33, 90) * mm});
            skLineSegment(sketch, "E88", {"start": v(0, -90) * mm, "end": v(0, -120) * mm});
            skPoint(sketch, "E88.endSnap0", {"position": v(0, -90) * mm});
            skCircle(sketch, "E89", {"center": v(0, -120) * mm, "radius": 6 * mm});
            skArc(sketch, "E90", {"start": v(15, -120) * mm, "mid": v(0, -135) * mm, "end": v(-15, -120) * mm});
            skLineSegment(sketch, "E91", {"start": v(-15, -120) * mm, "end": v(-15, -108) * mm});
            skLineSegment(sketch, "E92", {"start": v(15, -120) * mm, "end": v(15, -108) * mm});
            skLineSegment(sketch, "E93", {"start": v(0, -90) * mm, "end": v(33, -90) * mm});
            skLineSegment(sketch, "E94", {"start": v(0, -90) * mm, "end": v(-33, -90) * mm});
            skLineSegment(sketch, "E95", {"start": v(15, -108) * mm, "end": v(33, -90) * mm});
            skLineSegment(sketch, "E96", {"start": v(-15, -108) * mm, "end": v(-33, -90) * mm});
            skLineSegment(sketch, "E97", {"start": v(-33, -90) * mm, "end": v(-70, -90) * mm});
            skLineSegment(sketch, "E98", {"start": v(33, -90) * mm, "end": v(70, -90) * mm});
            skLineSegment(sketch, "E99", {"start": v(80, -80) * mm, "end": v(80, 80) * mm});
            skLineSegment(sketch, "E100", {"start": v(-80, -80) * mm, "end": v(-80, 80) * mm});
            skLineSegment(sketch, "E101", {"start": v(-33, 90) * mm, "end": v(-70, 90) * mm});
            skLineSegment(sketch, "E102", {"start": v(33, 90) * mm, "end": v(70, 90) * mm});
            skSolve(sketch);
        }
        {
            var Q0;
            Q0=makeQuery(id+"F16.imprint","IMPRINT",FACE,{"disambiguationData":[TD([[makeQuery(id+"F16.imprint","IMPRINT",EDGE,{"derivedFrom":sQuery(id+"F16.wireOp",EDGE,"E80")}),-1.0]])]});
            var Q1;
            Q1=makeQuery(id+"F16.imprint","IMPRINT",FACE,{"disambiguationData":[TD([[makeQuery(id+"F16.imprint","IMPRINT",EDGE,{"derivedFrom":sQuery(id+"F16.wireOp",EDGE,"E89")}),-1.0]])]});
            var Q2;
            Q2=makeQuery(id+"F16.imprint","IMPRINT",FACE,{"disambiguationData":[TD([[makeQuery(id+"F16.imprint","IMPRINT",EDGE,{"derivedFrom":sQuery(id+"F16.wireOp",EDGE,"E81")}),-1.0]])]});
            var Q3;
            Q3=makeQuery(id+"F2.opExtrude","CAP_FACE",FACE,{"disambiguationData":[OSD([sQuery(id+"F0.wireOp",EDGE,"E12"),sQuery(id+"F0.wireOp",EDGE,"E13"),sQuery(id+"F0.wireOp",EDGE,"E14"),sQuery(id+"F0.wireOp",EDGE,"E15"),sQuery(id+"F0.wireOp",EDGE,"E17.filletArc"),sQuery(id+"F0.wireOp",EDGE,"E18.filletArc"),sQuery(id+"F0.wireOp",EDGE,"E19.filletArc"),sQuery(id+"F0.wireOp",EDGE,"E20.filletArc"),sQuery(id+"F0.wireOp",EDGE,"E25.0"),sQuery(id+"F0.wireOp",EDGE,"E25.1"),sQuery(id+"F0.wireOp",EDGE,"E25.2"),sQuery(id+"F0.wireOp",EDGE,"E25.3"),sQuery(id+"F0.wireOp",EDGE,"E25.4"),sQuery(id+"F0.wireOp",EDGE,"E25.5"),sQuery(id+"F0.wireOp",EDGE,"E25.6"),sQuery(id+"F0.wireOp",EDGE,"E25.7")])],"isStart":false});
            extrude(context, id + "F17", {"entities" : qUnion([Q0, Q1, Q2]), "endBound" : BoundingType.UP_TO_SURFACE, "depth" : 25 * mm, "endBoundEntityFace" : qUnion([Q3]), "offsetDistance" : 25 * mm});
        }
    });
